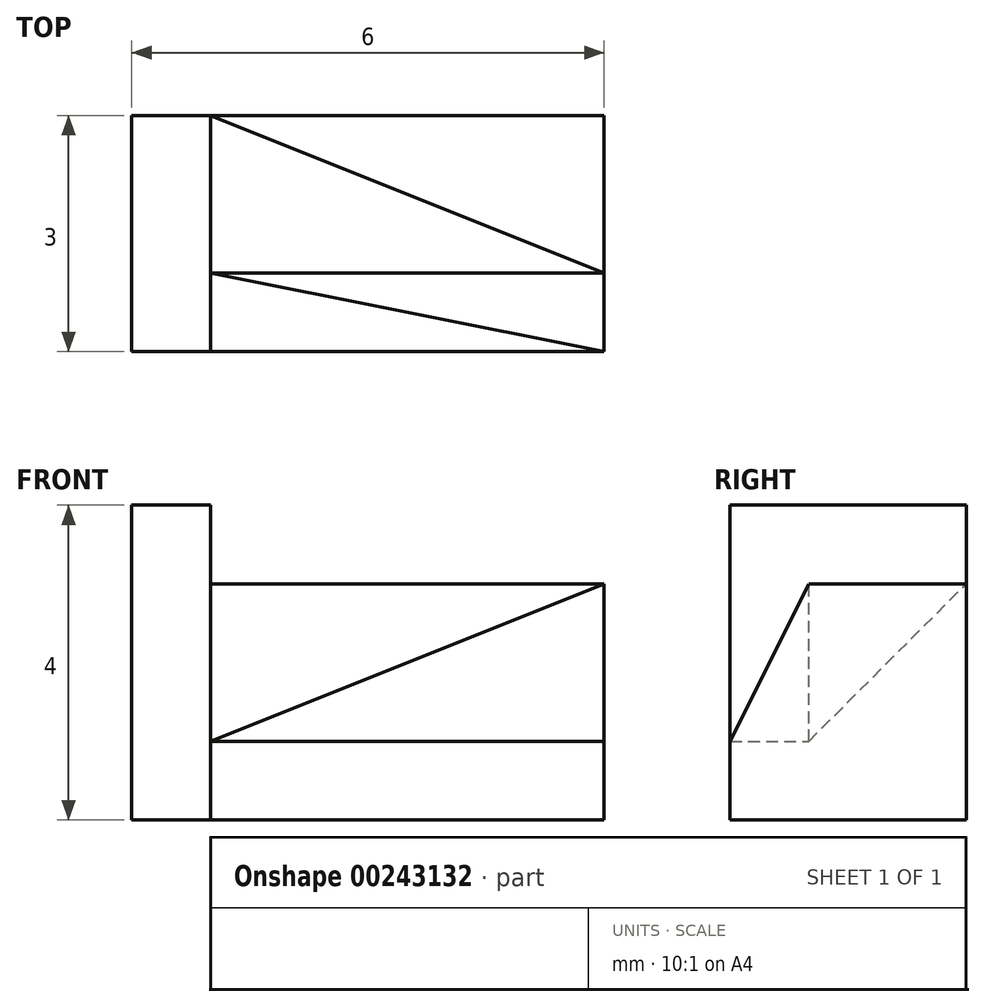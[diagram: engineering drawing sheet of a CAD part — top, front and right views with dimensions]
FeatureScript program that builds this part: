
annotation { "Feature Type Name" : "Feature", "Feature Type Description" : "" }
export const myFeature = defineFeature(function(context is Context, id is Id, definition is map)
    precondition{}
    {
        {
            var Q0;
            Q0=qCreatedBy(makeId("Front.planeOp"),FACE);
            var sketch = newSketch(context, id + "F0", { "sketchPlane" : qUnion([Q0])});
            skLineSegment(sketch, "E0.bottom", {"start": v(0, 0) * mm, "end": v(5, 0) * mm});
            skLineSegment(sketch, "E0.top", {"start": v(0, 3) * mm, "end": v(5, 3) * mm});
            skLineSegment(sketch, "E0.left", {"start": v(0, 0) * mm, "end": v(0, 3) * mm});
            skLineSegment(sketch, "E0.right", {"start": v(5, 0) * mm, "end": v(5, 3) * mm});
            skSolve(sketch);
        }
        {
            var Q0;
            Q0 = qSketchRegion(id + "F0", true);
            extrude(context, id + "F1", {"entities" : qUnion([Q0]), "depth" : 3 * mm});
        }
        {
            var Q0;
            Q0=makeQuery(id+"F1.opExtrude","SWEPT_FACE",FACE,{"disambiguationData":[OSD([sQuery(id+"F0.wireOp",EDGE,"E0.top")])]});
            var sketch = newSketch(context, id + "F2", { "sketchPlane" : qUnion([Q0])});
            skLineSegment(sketch, "E1", {"start": v(0, -3) * mm, "end": v(0, -2) * mm});
            skLineSegment(sketch, "E2", {"start": v(0, -2) * mm, "end": v(5, -3) * mm});
            skLineSegment(sketch, "E3", {"start": v(5, -3) * mm, "end": v(0, -3) * mm});
            skSolve(sketch);
        }
        {
            var Q0;
            Q0 = qSketchRegion(id + "F2", true);
            extrude(context, id + "F3", {"entities" : qUnion([Q0]), "operationType" : NewBodyOperationType.REMOVE, "oppositeDirection" : true, "depth" : 2 * mm});
        }
        {
            var Q0;
            Q0=makeQuery(id+"F1.opExtrude","SWEPT_FACE",FACE,{"disambiguationData":[OSD([sQuery(id+"F0.wireOp",EDGE,"E0.right")])]});
            var sketch = newSketch(context, id + "F4", { "sketchPlane" : qUnion([Q0])});
            skLineSegment(sketch, "E4", {"start": v(-3, 3) * mm, "end": v(-3, 1) * mm});
            skLineSegment(sketch, "E5", {"start": v(-3, 1) * mm, "end": v(-2, 3) * mm});
            skLineSegment(sketch, "E6", {"start": v(-2, 3) * mm, "end": v(-3, 3) * mm});
            skSolve(sketch);
        }
        {
            var Q0;
            Q0 = qSketchRegion(id + "F4", true);
            extrude(context, id + "F5", {"entities" : qUnion([Q0]), "operationType" : NewBodyOperationType.REMOVE, "oppositeDirection" : true, "depth" : 5 * mm});
        }
        {
            var Q0;
            Q0=makeQuery(id+"F3.boolean.opBoolean","COPY",VERTEX,{"derivedFrom":makeQuery(id+"F3.opExtrude","CAP_VERTEX",VERTEX,{"disambiguationData":[OSD([sQuery(id+"F0.wireOp",EDGE,"E0.top"),sQuery(id+"F0.wireOp",EDGE,"E0.left"),sQuery(id+"F2.wireOp",EDGE,"E1"),sQuery(id+"F2.wireOp",EDGE,"E2")])],"isStart":false})});
            var Q1;
            {var subQ0=sQuery(id+"F0.wireOp",EDGE,"E0.right");Q1=makeQuery(id+"F5.boolean.opBoolean","MERGE",VERTEX,{"derivedFrom":[makeQuery(id+"F3.boolean.opBoolean","COPY",VERTEX,{"derivedFrom":makeQuery(id+"F3.opExtrude","CAP_VERTEX",VERTEX,{"disambiguationData":[OSD([sQuery(id+"F0.wireOp",EDGE,"E0.top"),subQ0,sQuery(id+"F2.wireOp",EDGE,"E2"),sQuery(id+"F2.wireOp",EDGE,"E3")])],"isStart":false})}),makeQuery(id+"F5.opExtrude","CAP_VERTEX",VERTEX,{"disambiguationData":[OSD([subQ0,sQuery(id+"F4.wireOp",EDGE,"E4"),sQuery(id+"F4.wireOp",EDGE,"E5")])],"isStart":true})]});}
            var Q2;
            Q2=makeQuery(id+"F5.boolean.opBoolean","COPY",VERTEX,{"derivedFrom":makeQuery(id+"F5.opExtrude","CAP_VERTEX",VERTEX,{"disambiguationData":[OSD([sQuery(id+"F0.wireOp",EDGE,"E0.top"),sQuery(id+"F0.wireOp",EDGE,"E0.right"),sQuery(id+"F4.wireOp",EDGE,"E5"),sQuery(id+"F4.wireOp",EDGE,"E6")])],"isStart":true})});
            cPlane(context, id + "F6", {"entities" : qUnion([Q0, Q1, Q2]), "cplaneType" : CPlaneType.THREE_POINT, "offset" : 25 * mm, "width" : 150 * mm, "height" : 150 * mm});
        }
        {
            var Q0;
            Q0=qCreatedBy(id+"F6.planeOp",FACE);
            var sketch = newSketch(context, id + "F7", { "sketchPlane" : qUnion([Q0])});
            skPoint(sketch, "E7.0", {"position": v(-0.4, 0) * mm});
            skPoint(sketch, "E7.1", {"position": v(-5.47, 1.79) * mm});
            skPoint(sketch, "E7.2", {"position": v(-5.47, -0.45) * mm});
            skLineSegment(sketch, "E8", {"start": v(-0.4, 0) * mm, "end": v(-5.47, -0.45) * mm});
            skLineSegment(sketch, "E9", {"start": v(-5.47, -0.45) * mm, "end": v(-5.47, 1.79) * mm});
            skLineSegment(sketch, "E10", {"start": v(-0.4, 0) * mm, "end": v(0, 0.3) * mm});
            skLineSegment(sketch, "E11", {"start": v(0, 0.3) * mm, "end": v(-5.47, 1.79) * mm});
            skSolve(sketch);
        }
        {
            var Q0;
            Q0 = qSketchRegion(id + "F7", true);
            extrude(context, id + "F8", {"entities" : qUnion([Q0]), "operationType" : NewBodyOperationType.REMOVE, "oppositeDirection" : true, "depth" : 25 * mm});
        }
        {
            var Q0;
            Q0=makeQuery(id+"F1.opExtrude","CAP_VERTEX",VERTEX,{"disambiguationData":[OSD([sQuery(id+"F0.wireOp",EDGE,"E0.top"),sQuery(id+"F0.wireOp",EDGE,"E0.left")])],"isStart":true});
            var Q1;
            Q1=makeQuery(id+"F8.boolean.opBoolean","MERGE",VERTEX,{"derivedFrom":[makeQuery(id+"F3.boolean.opBoolean","COPY",VERTEX,{"derivedFrom":makeQuery(id+"F3.opExtrude","CAP_VERTEX",VERTEX,{"disambiguationData":[OSD([sQuery(id+"F0.wireOp",EDGE,"E0.top"),sQuery(id+"F0.wireOp",EDGE,"E0.left"),sQuery(id+"F2.wireOp",EDGE,"E1"),sQuery(id+"F2.wireOp",EDGE,"E2")])],"isStart":false})}),makeQuery(id+"F8.opExtrude","CAP_VERTEX",VERTEX,{"disambiguationData":[OSD([sQuery(id+"F7.wireOp",EDGE,"E8"),sQuery(id+"F7.wireOp",EDGE,"CYTQ7vWQ-Wvvr-tjsT-wWG0-EdrhFYRdAYPr")])],"isStart":true})]});
            var Q2;
            Q2=makeQuery(id+"F8.boolean.opBoolean","MERGE",VERTEX,{"derivedFrom":[makeQuery(id+"F5.boolean.opBoolean","COPY",VERTEX,{"derivedFrom":makeQuery(id+"F5.opExtrude","CAP_VERTEX",VERTEX,{"disambiguationData":[OSD([sQuery(id+"F0.wireOp",EDGE,"E0.top"),sQuery(id+"F0.wireOp",EDGE,"E0.right"),sQuery(id+"F4.wireOp",EDGE,"E5"),sQuery(id+"F4.wireOp",EDGE,"E6")])],"isStart":true})}),makeQuery(id+"F8.opExtrude","CAP_VERTEX",VERTEX,{"disambiguationData":[OSD([sQuery(id+"F7.wireOp",EDGE,"E9"),sQuery(id+"F7.wireOp",EDGE,"CYTQ7vWQ-Wvvr-tjsT-wWG0-EdrhFYRdAYPr")])],"isStart":true})]});
            cPlane(context, id + "F9", {"entities" : qUnion([Q0, Q1, Q2]), "cplaneType" : CPlaneType.THREE_POINT, "offset" : 25 * mm, "width" : 150 * mm, "height" : 150 * mm});
        }
        {
            var Q0;
            Q0=qCreatedBy(id+"F9.planeOp",FACE);
            var sketch = newSketch(context, id + "F10", { "sketchPlane" : qUnion([Q0])});
            skPoint(sketch, "E12.0", {"position": v(-0.58, 2.12) * mm});
            skPoint(sketch, "E12.1", {"position": v(-5.77, 0.7) * mm});
            skPoint(sketch, "E12.2", {"position": v(-0.58, -0.7) * mm});
            skLineSegment(sketch, "E13", {"start": v(-0.58, 2.12) * mm, "end": v(-5.77, 0.7) * mm});
            skLineSegment(sketch, "E14", {"start": v(-0.58, -0.7) * mm, "end": v(-0.58, 2.12) * mm});
            skLineSegment(sketch, "E15", {"start": v(-0.58, -0.7) * mm, "end": v(-5.77, 0.7) * mm});
            skSolve(sketch);
        }
        {
            var Q0;
            Q0 = qSketchRegion(id + "F10", true);
            extrude(context, id + "F11", {"entities" : qUnion([Q0]), "operationType" : NewBodyOperationType.REMOVE, "oppositeDirection" : true, "depth" : 25 * mm});
        }
        {
            var Q0;
            Q0=makeQuery(id+"F1.opExtrude","SWEPT_FACE",FACE,{"disambiguationData":[OSD([sQuery(id+"F0.wireOp",EDGE,"E0.bottom")])]});
            var sketch = newSketch(context, id + "F12", { "sketchPlane" : qUnion([Q0])});
            skLineSegment(sketch, "E16", {"start": v(0, 0) * mm, "end": v(0, 3) * mm});
            skLineSegment(sketch, "E17", {"start": v(0, 3) * mm, "end": v(-1, 3) * mm});
            skLineSegment(sketch, "E18", {"start": v(-1, 3) * mm, "end": v(-1, 0) * mm});
            skLineSegment(sketch, "E19", {"start": v(-1, 0) * mm, "end": v(0, 0) * mm});
            skSolve(sketch);
        }
        {
            var Q0;
            Q0 = qSketchRegion(id + "F12", true);
            extrude(context, id + "F13", {"entities" : qUnion([Q0]), "oppositeDirection" : true, "depth" : 4 * mm});
        }
    });
